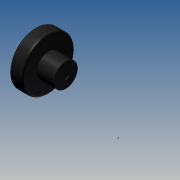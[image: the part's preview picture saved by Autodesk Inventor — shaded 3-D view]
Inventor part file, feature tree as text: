
AUTODESK INVENTOR PART (.ipt)
format: ipt  version: 2011 (Build 150239000, 239)  size: 114,688 bytes
history: native  units: mm
features: sketch x4, extrude x2, revolve x1, fillet x1
ambient origin geometry x8: Origin, YZ Plane, XZ Plane, XY Plane, X Axis, Y Axis, Z Axis, Center Point
bodies: Solid1 (feature_tree)
feature tree (8):
  sketch  "Sketch1"  dims[d87=12.03mm d90=3.175mm d92=90.0deg]
  revolve  "Revolution1"  [1 undecoded]
  sketch  "Sketch10"  dims[d100=0.1mm d101=0.0mm]
  fillet  "Fillet11"  [1 undecoded]
  extrude  "Extrusion7"  Depth=2.1mm TaperAngle=0.0deg
  extrude  "Extrusion10"  [1 undecoded]
  sketch  "Sketch9"  dims[d93=0.2mm d94=2.1mm d95=0.0mm]
  sketch  "Sketch12"
note: 3 required parameter values undecoded (feature->parameter linkage not recoverable at this tier; creation-order binding heuristic only, values carry confidence <= 0.55)